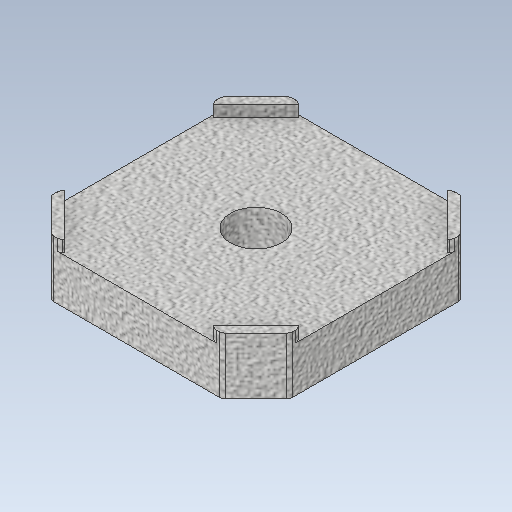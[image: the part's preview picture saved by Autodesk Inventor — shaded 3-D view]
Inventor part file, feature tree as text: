
AUTODESK INVENTOR PART (.ipt)
format: ipt  version: 2020 (Build 240168000, 168)  size: 360,448 bytes
history: native  units: mm
features: sketch x8, extrude x6, mirror x4, fillet x4, projected_geometry x2, chamfer x1
ambient origin geometry x8: Origin, YZ Plane, XZ Plane, XY Plane, X Axis, Y Axis, Z Axis, Center Point
bodies: Solid1 (feature_tree)
feature tree (25):
  extrude  "Extrusion1"  Depth=42.0mm
  sketch  "Sketch2"  dims[d4=6.0mm d5=2.0mm d6=45.0deg d7=2.0mm d8=0.0mm d10=1.0mm d11=1.0mm]
  chamfer  "Chamfer1"  Distance=8.0mm
  extrude  "Extrusion2"  Depth=2.0mm TaperAngle=0.0deg
  mirror  "Mirror1"
  mirror  "Mirror2"
  fillet  "Fillet2"  Radius=1.0mm
  fillet  "Fillet3"  Radius=1.0mm
  extrude  "Extrusion3"  Depth=1.0mm
  extrude  "Extrusion4"  Depth=22.0mm
  extrude  "Extrusion5"  Depth=2.5mm TaperAngle=0.0deg
  sketch  "Sketch7"  dims[d25=5.5mm]
  extrude  "Extrusion6"  Depth=2.5mm TaperAngle=0.0deg
  mirror  "Mirror3"
  mirror  "Mirror4"
  fillet  "Fillet4"  Radius=3.0mm
  fillet  "Fillet5"  Radius=5.5mm
  sketch  "Sketch1"  dims[d0=42.0mm d1=42.0mm d2=8.0mm d3=0.0mm]
  sketch  "Sketch3"  dims[d12=1.0mm d13=1.0mm]
  projected_geometry  "Projected Loop1"
  sketch  "Sketch4"  dims[d14=32.0mm d15=22.0mm]
  sketch  "Sketch5"  dims[d16=1.0mm d17=0.0mm d18=2.5mm d19=0.0mm]
  projected_geometry  "Projected Loop2"
  sketch  "Sketch6"  dims[d20=9.0mm d21=2.5mm d22=0.0mm d23=3.0mm d24=5.5mm]
  sketch  "Sketch8"  dims[d26=5.0mm d27=0.0mm d28=0.5mm d29=0.5mm]
